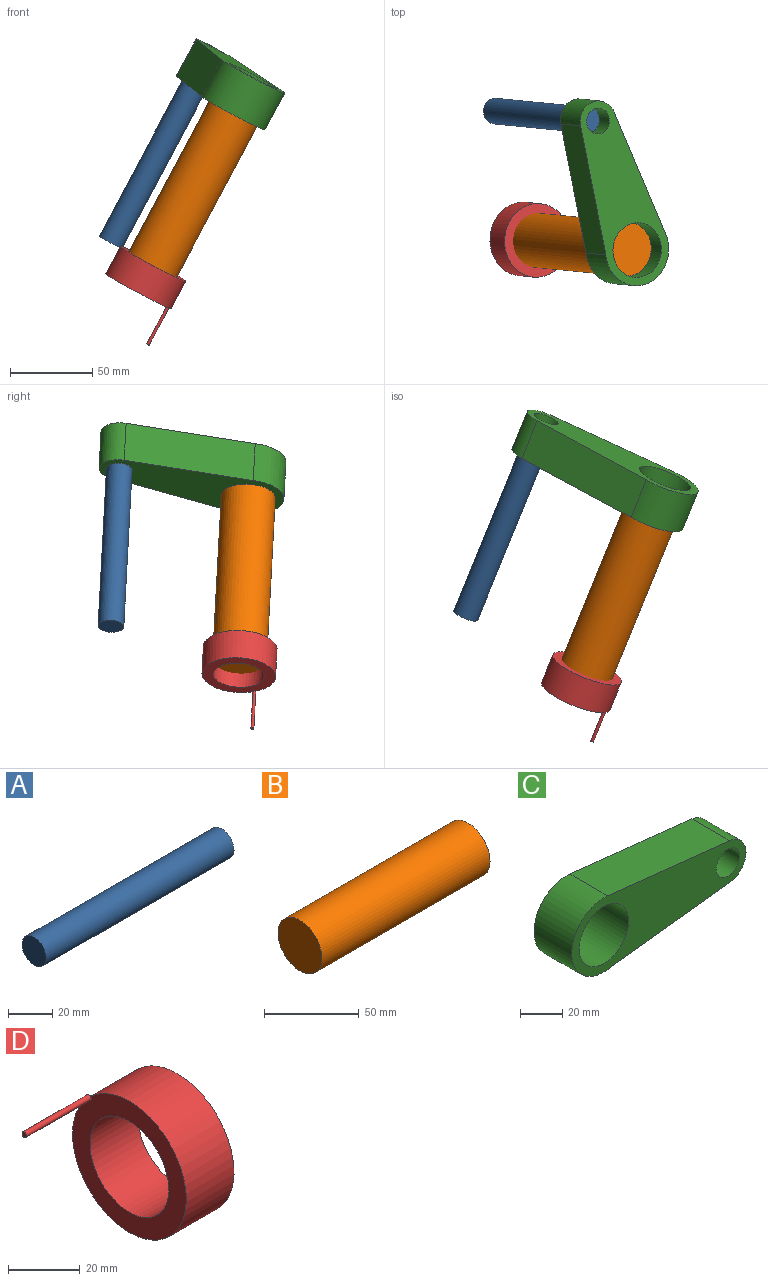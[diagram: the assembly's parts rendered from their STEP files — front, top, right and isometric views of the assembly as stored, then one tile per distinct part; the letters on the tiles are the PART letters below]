
ASSEMBLY  parts=4 mates=4
PART A: 3 faces, bbox 120.6x15.5x15.5 mm
  f0: cylinder r=7.77mm len=120.59mm, axis (-1,0,0), area 5887.8mm2, adj f1,f2
  f1: plane 15.54x15.54mm, normal (-1,0,0), area 189.7mm2, adj f0
  f2: plane 15.54x15.54mm, normal (1,0,0), area 189.7mm2, adj f0
PART B: 3 faces, bbox 125.8x32.8x32.8 mm
  f0: plane 32.81x32.81mm, normal (-1,0,0), area 845.5mm2, adj f1
  f1: cylinder r=16.4mm len=125.77mm, axis (-1,0,0), area 12963.9mm2, adj f0,f2
  f2: plane 32.81x32.81mm, normal (1,0,0), area 845.5mm2, adj f1
PART C: 8 faces, bbox 117.4x25.4x43.3 mm
  f0: cylinder r=21.65mm len=43.31mm, axis (0,1,0), area 1914.1mm2, adj f1,f3,f4,f5
  f1: plane 80.12x25.4mm, normal (0.12,0,-0.99), area 2048.8mm2, adj f0,f2,f4,f5
  f2: cylinder r=12.28mm len=25.4mm, axis (0,1,0), area 910.5mm2, adj f1,f3,f4,f5
  f3: plane 82.16x25.4mm, normal (0.11,0,0.99), area 2099.1mm2, adj f0,f2,f4,f5
  f4: plane 117.35x43.31mm, normal (0,-1,0), area 2757.4mm2, adj f0,f1,f2,f3,f6,f7
  f5: plane 117.35x43.31mm, normal (0,1,0), area 2757.4mm2, adj f0,f1,f2,f3,f6,f7
  f6: cylinder r=16.63mm len=33.25mm, axis (0,-1,0), area 2653.4mm2, adj f4,f5
  f7: cylinder r=7.82mm len=25.4mm, axis (0,-1,0), area 1247.4mm2, adj f4,f5
PART D: 7 faces, bbox 44.2x44.7x44.7 mm
  f0: cylinder r=22.35mm len=44.7mm, axis (-1,0,0), area 2639.7mm2, adj f1,f3,f4
  f1: plane 44.7x44.7mm, normal (-1,0,0), area 814.2mm2, adj f0,f2,f5
  f2: cylinder r=15.49mm len=30.99mm, axis (-1,0,0), area 1829.8mm2, adj f1,f3
  f3: plane 44.7x44.7mm, normal (1,0,0), area 815.4mm2, adj f0,f2
  f4: plane 1.53x1.51mm, normal (1,0,0), area 1.2mm2, adj f0,f5
  f5: cylinder r=0.88mm len=25.4mm, axis (1,0,0), area 141mm2, adj f1,f4,f6
  f6: plane 1.77x1.77mm, normal (-1,0,0), area 2.5mm2, adj f5
PLACE A rot(axis=(-0.68,-0.58,-0.44),89.3deg) t=(-190.22,-72.19,75.29)mm
PLACE B rot(axis=(0.81,-0.35,0.47),122.8deg) t=(-164.21,-159.47,55.46)mm
PLACE C rot(axis=(0.56,0.67,0.49),151.7deg) t=(-177.27,-95.6,159.58)mm
PLACE D rot(axis=(-0.85,-0.07,-0.52),161.1deg) t=(-196.09,-134.36,47.62)mm
MATE planar A.f0 <-> A.f0  axis (-0.47,0.05,-0.88) through (-220.71,-49.83,33.96)mm
MATE fastened B.f1 <-> C.f0  axis (-0.47,0.05,-0.88) through (-140.3,-133.67,123.43)mm
MATE fastened C.f2 <-> A.f0  axis (-0.47,0.05,-0.88) through (-164.03,-55.49,140.25)mm
MATE fastened D.f0 <-> B.f1  axis (-0.47,0.05,-0.88) through (-199.41,-127.76,12.57)mm
